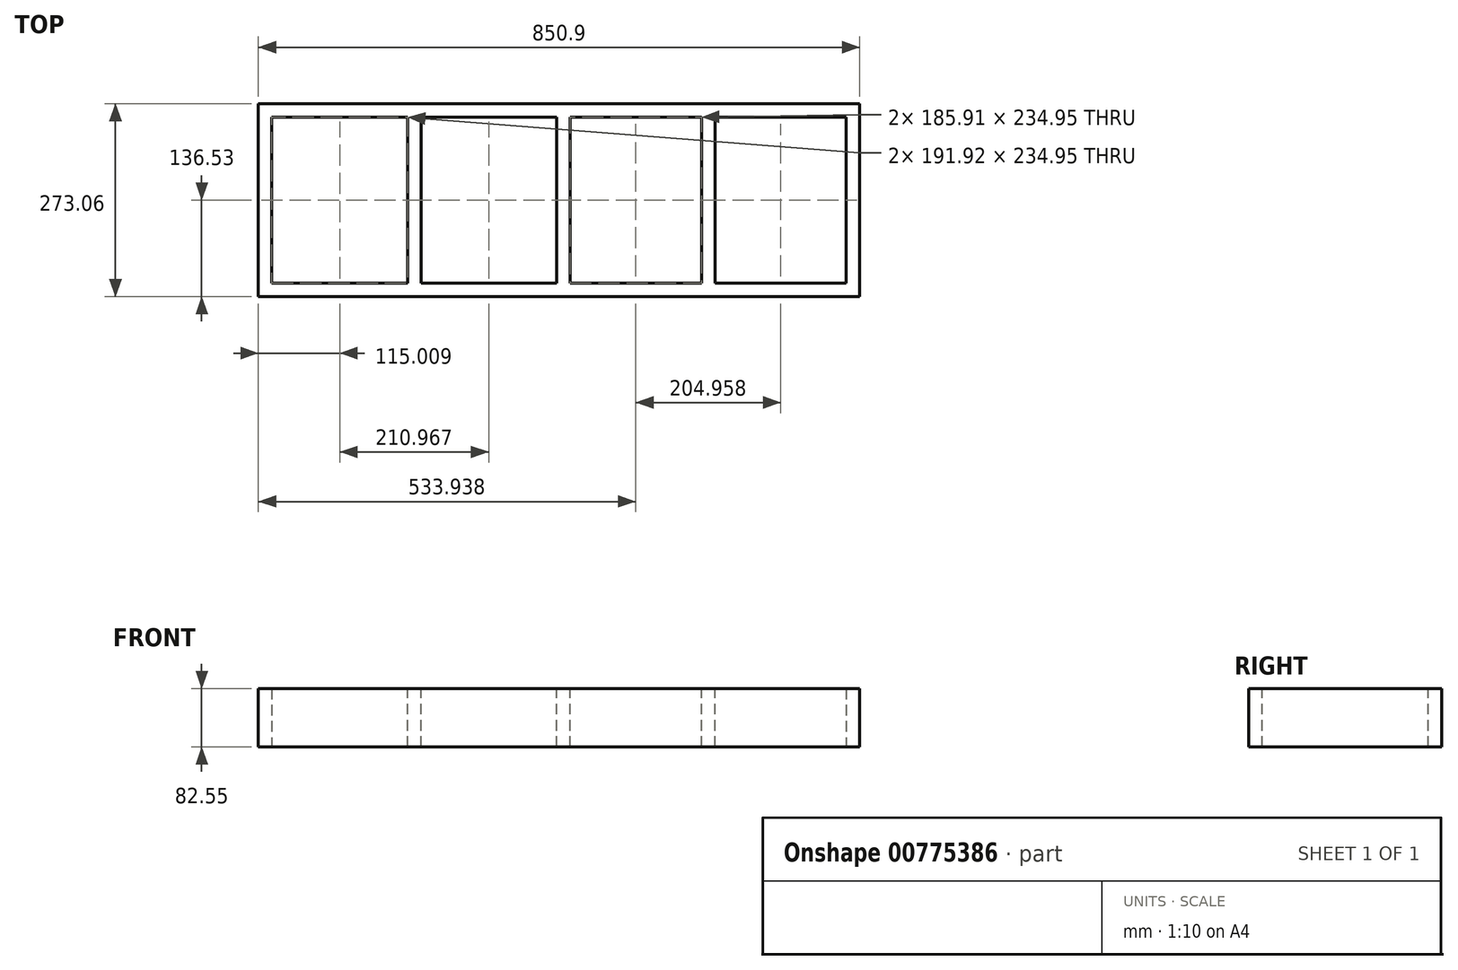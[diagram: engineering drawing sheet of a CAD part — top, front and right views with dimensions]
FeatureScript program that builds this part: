
annotation { "Feature Type Name" : "Feature", "Feature Type Description" : "" }
export const myFeature = defineFeature(function(context is Context, id is Id, definition is map)
    precondition{}
    {
        {
            var Q0;
            Q0=qCreatedBy(makeId("Top.planeOp"),FACE);
            var sketch = newSketch(context, id + "F0", { "sketchPlane" : qUnion([Q0])});
            skLineSegment(sketch, "E0.bottom", {"start": v(425.45, 136.53) * mm, "end": v(-425.45, 136.53) * mm});
            skLineSegment(sketch, "E0.top", {"start": v(425.45, -136.53) * mm, "end": v(-425.45, -136.53) * mm});
            skLineSegment(sketch, "E0.left", {"start": v(425.45, 136.53) * mm, "end": v(425.45, -136.53) * mm});
            skLineSegment(sketch, "E0.right", {"start": v(-425.45, 136.53) * mm, "end": v(-425.45, -136.53) * mm});
            skPoint(sketch, "E0.middle", {"position": v(0, 0) * mm});
            skSolve(sketch);
        }
        {
            var Q0;
            Q0=makeQuery(id+"F0.imprint","IMPRINT",FACE,{"disambiguationData":[TD([[makeQuery(id+"F0.imprint","IMPRINT",EDGE,{"derivedFrom":sQuery(id+"F0.wireOp",EDGE,"E0.bottom")}),1.0]])]});
            var sketch = newSketch(context, id + "F1", { "sketchPlane" : qUnion([Q0])});
            skLineSegment(sketch, "E1.bottom", {"start": v(406.4, 117.48) * mm, "end": v(-406.4, 117.48) * mm});
            skLineSegment(sketch, "E1.top", {"start": v(406.4, -117.48) * mm, "end": v(-406.4, -117.48) * mm});
            skLineSegment(sketch, "E1.left", {"start": v(406.4, 117.48) * mm, "end": v(406.4, -117.48) * mm});
            skLineSegment(sketch, "E1.right", {"start": v(-406.4, 117.48) * mm, "end": v(-406.4, -117.48) * mm});
            skPoint(sketch, "E1.middle", {"position": v(0, 0) * mm});
            skSolve(sketch);
        }
        {
            var Q0;
            Q0=makeQuery(id+"F1.imprint","IMPRINT",FACE,{"disambiguationData":[TD([[makeQuery(id+"F1.imprint","IMPRINT",EDGE,{"derivedFrom":sQuery(id+"F1.wireOp",EDGE,"E1.bottom")}),-1.0]])]});
            extrude(context, id + "F2", {"entities" : qUnion([Q0]), "depth" : 82.55 * mm, "offsetDistance" : 25.4 * mm});
        }
        {
            var Q0;
            Q0=makeQuery(id+"F2.opExtrude","CAP_FACE",FACE,{"disambiguationData":[OSD([sQuery(id+"F0.wireOp",EDGE,"E0.bottom"),sQuery(id+"F0.wireOp",EDGE,"E0.top"),sQuery(id+"F0.wireOp",EDGE,"E0.left"),sQuery(id+"F0.wireOp",EDGE,"E0.right"),sQuery(id+"F1.wireOp",EDGE,"E1.bottom"),sQuery(id+"F1.wireOp",EDGE,"E1.top"),sQuery(id+"F1.wireOp",EDGE,"E1.left"),sQuery(id+"F1.wireOp",EDGE,"E1.right")])],"isStart":false});
            var sketch = newSketch(context, id + "F3", { "sketchPlane" : qUnion([Q0])});
            skLineSegment(sketch, "E2.bottom", {"start": v(15.53, 117.48) * mm, "end": v(-3.52, 117.48) * mm});
            skLineSegment(sketch, "E2.top", {"start": v(15.53, -117.48) * mm, "end": v(-3.52, -117.48) * mm});
            skLineSegment(sketch, "E2.left", {"start": v(15.53, 117.48) * mm, "end": v(15.53, -117.48) * mm});
            skLineSegment(sketch, "E2.right", {"start": v(-3.52, 117.48) * mm, "end": v(-3.52, -117.48) * mm});
            skPoint(sketch, "E2.middle", {"position": v(6, 0) * mm});
            skSolve(sketch);
        }
        {
            var Q0;
            Q0=makeQuery(id+"F3.imprint","IMPRINT",FACE,{"disambiguationData":[TD([[makeQuery(id+"F3.imprint","IMPRINT",EDGE,{"derivedFrom":sQuery(id+"F3.wireOp",EDGE,"E2.bottom")}),1.0]])]});
            extrude(context, id + "F4", {"entities" : qUnion([Q0]), "operationType" : NewBodyOperationType.ADD, "depth" : -82.55 * mm, "offsetDistance" : 25.4 * mm});
        }
        {
            var Q0;
            Q0=makeQuery(id+"F4.boolean.opBoolean","MERGE",FACE,{"derivedFrom":[makeQuery(id+"F2.opExtrude","CAP_FACE",FACE,{"disambiguationData":[OSD([sQuery(id+"F0.wireOp",EDGE,"E0.bottom"),sQuery(id+"F0.wireOp",EDGE,"E0.top"),sQuery(id+"F0.wireOp",EDGE,"E0.left"),sQuery(id+"F0.wireOp",EDGE,"E0.right"),sQuery(id+"F1.wireOp",EDGE,"E1.bottom"),sQuery(id+"F1.wireOp",EDGE,"E1.top"),sQuery(id+"F1.wireOp",EDGE,"E1.left"),sQuery(id+"F1.wireOp",EDGE,"E1.right")])],"isStart":false}),makeQuery(id+"F4.opExtrude","CAP_FACE",FACE,{"disambiguationData":[OSD([sQuery(id+"F3.wireOp",EDGE,"E2.bottom"),sQuery(id+"F3.wireOp",EDGE,"E2.top"),sQuery(id+"F3.wireOp",EDGE,"E2.left"),sQuery(id+"F3.wireOp",EDGE,"E2.right")])],"isStart":true})]});
            var sketch = newSketch(context, id + "F5", { "sketchPlane" : qUnion([Q0])});
            skLineSegment(sketch, "E3.bottom", {"start": v(-195.43, -204.31) * mm, "end": v(-214.48, -204.31) * mm});
            skLineSegment(sketch, "E3.top", {"start": v(-195.43, 439.26) * mm, "end": v(-214.48, 439.26) * mm});
            skLineSegment(sketch, "E3.left", {"start": v(-195.43, -204.31) * mm, "end": v(-195.43, 439.26) * mm});
            skLineSegment(sketch, "E3.right", {"start": v(-214.48, -204.31) * mm, "end": v(-214.48, 439.26) * mm});
            skPoint(sketch, "E3.middle", {"position": v(-204.96, 117.48) * mm});
            skSolve(sketch);
        }
        {
            var Q0;
            {var subQ0=sQuery(id+"F5.wireOp",EDGE,"E3.left");var subQ3=sQuery(id+"F1.wireOp",EDGE,"E1.right");var subQ4=sQuery(id+"F1.wireOp",EDGE,"E1.top");var subQ7=makeQuery(id+"F2.opExtrude","SWEPT_FACE",FACE,{"disambiguationData":[OSD([subQ3])]});var subQ9=makeQuery(id+"F4.boolean.opBoolean","SPLIT",EDGE,{"disambiguationData":[TD([subQ7])],"derivedFrom":makeQuery(id+"F2.opExtrude","CAP_EDGE",EDGE,{"disambiguationData":[OSD([subQ4])],"isStart":false})});var subQ10=makeQuery(id+"F5.imprint","INTERSECT",VERTEX,{"derivedFrom":[subQ9,subQ0]});Q0=makeQuery(id+"F5.imprint","IMPRINT",FACE,{"disambiguationData":[TD([[makeQuery(id+"F5.imprint","IMPRINT",EDGE,{"disambiguationData":[TD([[subQ10,-1.0]])],"derivedFrom":subQ0}),1.0]])]});}
            extrude(context, id + "F6", {"entities" : qUnion([Q0]), "operationType" : NewBodyOperationType.ADD, "depth" : -82.55 * mm, "offsetDistance" : 25.4 * mm});
        }
        {
            var Q0;
            {var subQ0=sQuery(id+"F1.wireOp",EDGE,"E1.top");var subQ1=sQuery(id+"F1.wireOp",EDGE,"E1.bottom");Q0=makeQuery(id+"F6.boolean.opBoolean","MERGE",FACE,{"derivedFrom":[makeQuery(id+"F4.boolean.opBoolean","MERGE",FACE,{"derivedFrom":[makeQuery(id+"F2.opExtrude","CAP_FACE",FACE,{"disambiguationData":[OSD([sQuery(id+"F0.wireOp",EDGE,"E0.bottom"),sQuery(id+"F0.wireOp",EDGE,"E0.top"),sQuery(id+"F0.wireOp",EDGE,"E0.left"),sQuery(id+"F0.wireOp",EDGE,"E0.right"),subQ1,subQ0,sQuery(id+"F1.wireOp",EDGE,"E1.left"),sQuery(id+"F1.wireOp",EDGE,"E1.right")])],"isStart":false}),makeQuery(id+"F4.opExtrude","CAP_FACE",FACE,{"disambiguationData":[OSD([sQuery(id+"F3.wireOp",EDGE,"E2.bottom"),sQuery(id+"F3.wireOp",EDGE,"E2.top"),sQuery(id+"F3.wireOp",EDGE,"E2.left"),sQuery(id+"F3.wireOp",EDGE,"E2.right")])],"isStart":true})]}),makeQuery(id+"F6.opExtrude","CAP_FACE",FACE,{"disambiguationData":[OSD([subQ1,subQ0,sQuery(id+"F5.wireOp",EDGE,"E3.left"),sQuery(id+"F5.wireOp",EDGE,"E3.right")])],"isStart":true})]});}
            var sketch = newSketch(context, id + "F7", { "sketchPlane" : qUnion([Q0])});
            skLineSegment(sketch, "E4.bottom", {"start": v(220.5, -219.9) * mm, "end": v(201.44, -219.9) * mm});
            skLineSegment(sketch, "E4.top", {"start": v(220.5, 454.86) * mm, "end": v(201.44, 454.86) * mm});
            skLineSegment(sketch, "E4.left", {"start": v(220.5, -219.9) * mm, "end": v(220.5, 454.86) * mm});
            skLineSegment(sketch, "E4.right", {"start": v(201.44, -219.9) * mm, "end": v(201.44, 454.86) * mm});
            skPoint(sketch, "E4.middle", {"position": v(210.97, 117.48) * mm});
            skSolve(sketch);
        }
        {
            var Q0;
            {var subQ0=sQuery(id+"F7.wireOp",EDGE,"E4.left");var subQ3=sQuery(id+"F1.wireOp",EDGE,"E1.left");var subQ4=sQuery(id+"F1.wireOp",EDGE,"E1.top");var subQ7=makeQuery(id+"F2.opExtrude","SWEPT_FACE",FACE,{"disambiguationData":[OSD([subQ3])]});var subQ9=makeQuery(id+"F4.boolean.opBoolean","SPLIT",EDGE,{"disambiguationData":[TD([subQ7])],"derivedFrom":makeQuery(id+"F2.opExtrude","CAP_EDGE",EDGE,{"disambiguationData":[OSD([subQ4])],"isStart":false})});var subQ10=makeQuery(id+"F7.imprint","INTERSECT",VERTEX,{"derivedFrom":[subQ9,subQ0]});Q0=makeQuery(id+"F7.imprint","IMPRINT",FACE,{"disambiguationData":[TD([[makeQuery(id+"F7.imprint","IMPRINT",EDGE,{"disambiguationData":[TD([[subQ10,-1.0]])],"derivedFrom":subQ0}),1.0]])]});}
            extrude(context, id + "F8", {"entities" : qUnion([Q0]), "operationType" : NewBodyOperationType.ADD, "depth" : -82.55 * mm, "offsetDistance" : 25.4 * mm});
        }
    });
